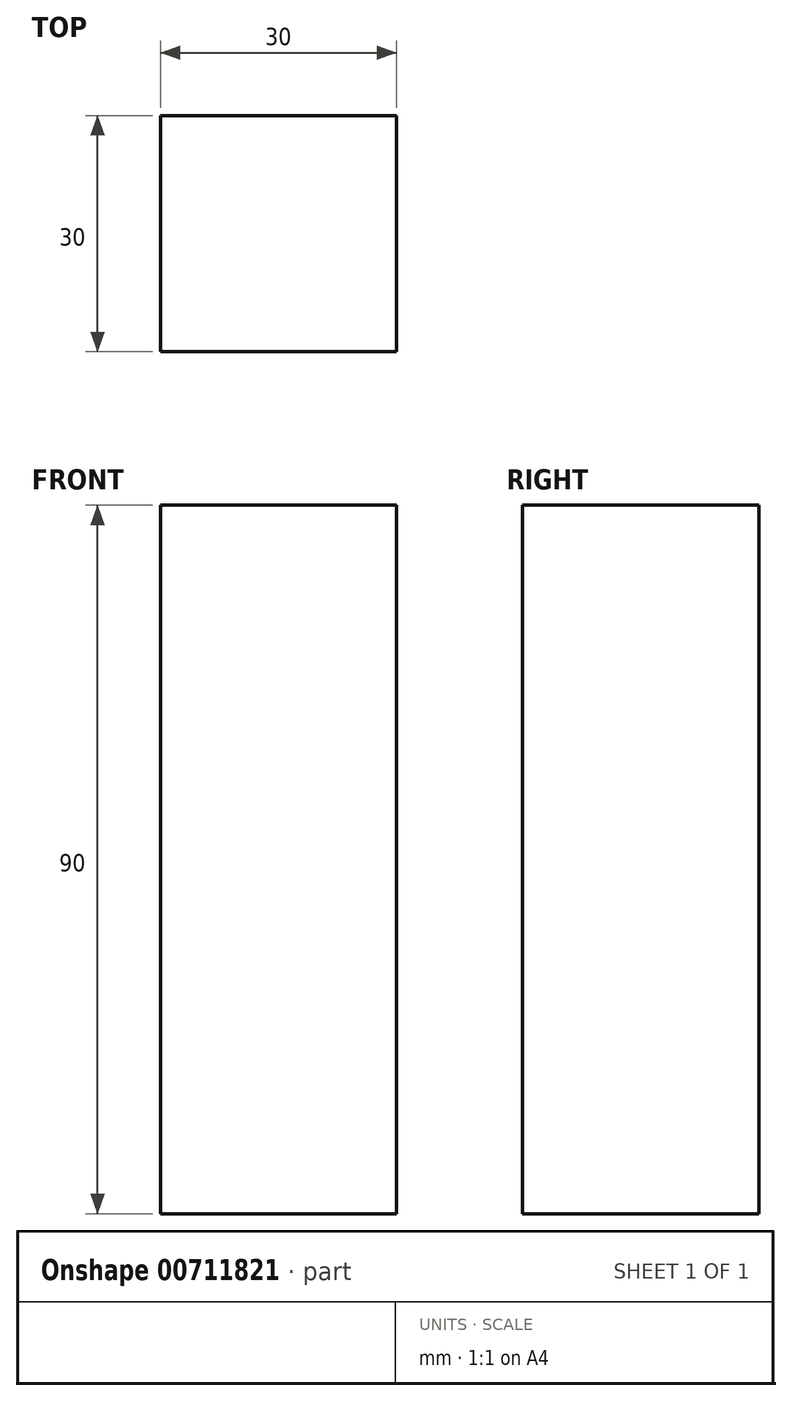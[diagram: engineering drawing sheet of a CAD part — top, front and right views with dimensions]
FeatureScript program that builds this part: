
annotation { "Feature Type Name" : "Feature", "Feature Type Description" : "" }
export const myFeature = defineFeature(function(context is Context, id is Id, definition is map)
    precondition{}
    {
        {
            var Q0;
            Q0=qCreatedBy(makeId("Top.planeOp"),FACE);
            var sketch = newSketch(context, id + "F0", { "sketchPlane" : qUnion([Q0])});
            skLineSegment(sketch, "E0.bottom", {"start": v(-9.4, 6.27) * mm, "end": v(20.6, 6.27) * mm});
            skLineSegment(sketch, "E0.top", {"start": v(-9.4, -23.73) * mm, "end": v(20.6, -23.73) * mm});
            skLineSegment(sketch, "E0.left", {"start": v(-9.4, 6.27) * mm, "end": v(-9.4, -23.73) * mm});
            skLineSegment(sketch, "E0.right", {"start": v(20.6, 6.27) * mm, "end": v(20.6, -23.73) * mm});
            skSolve(sketch);
        }
        {
            var Q0;
            Q0 = qSketchRegion(id + "F0", true);
            extrude(context, id + "F1", {"entities" : qUnion([Q0]), "depth" : 90 * mm, "offsetDistance" : 25.4 * mm});
        }
    });
